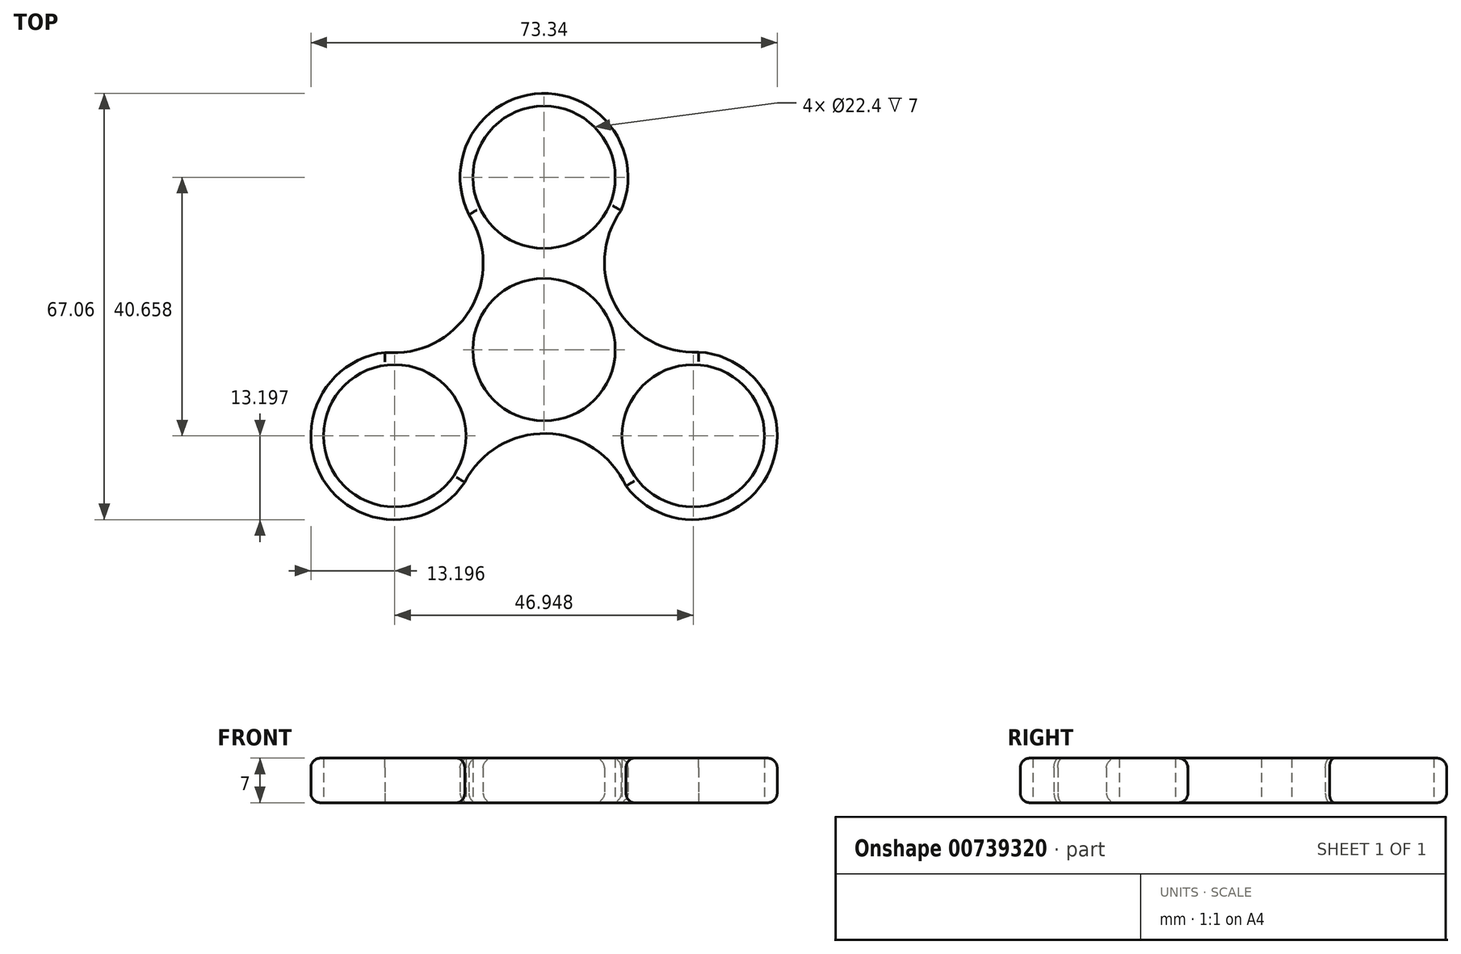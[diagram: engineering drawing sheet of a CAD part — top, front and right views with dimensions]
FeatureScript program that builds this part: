
annotation { "Feature Type Name" : "Feature", "Feature Type Description" : "" }
export const myFeature = defineFeature(function(context is Context, id is Id, definition is map)
    precondition{}
    {
        {
            var Q0;
            Q0=qCreatedBy(makeId("Top.planeOp"),FACE);
            var sketch = newSketch(context, id + "F0", { "sketchPlane" : qUnion([Q0])});
            skCircle(sketch, "E0", {"center": v(0, 0) * mm, "radius": 11.2 * mm});
            skArc(sketch, "E1", {"start": v(-11.26, 6.88) * mm, "mid": v(-11.45, 6.57) * mm, "end": v(-11.62, 6.26) * mm});
            skCircle(sketch, "E2", {"center": v(0, 27.1) * mm, "radius": 11.2 * mm});
            skArc(sketch, "E3", {"start": v(10.69, 19.36) * mm, "mid": v(0.33, 40.3) * mm, "end": v(-11.06, 19.9) * mm});
            skArc(sketch, "E4.1.0", {"start": v(-22.1, -0.42) * mm, "mid": v(-35.07, -19.86) * mm, "end": v(-11.7, -19.53) * mm});
            skCircle(sketch, "E4.1.1", {"center": v(-23.47, -13.55) * mm, "radius": 11.2 * mm});
            skArc(sketch, "E4.2.0", {"start": v(11.42, -18.94) * mm, "mid": v(34.74, -20.44) * mm, "end": v(22.77, -0.37) * mm});
            skCircle(sketch, "E4.2.1", {"center": v(23.47, -13.55) * mm, "radius": 11.2 * mm});
            skArc(sketch, "E5", {"start": v(12.13, 21.9) * mm, "mid": v(11.23, 6.94) * mm, "end": v(24.3, -0.38) * mm});
            skArc(sketch, "E6.1.0", {"start": v(-25.02, -0.44) * mm, "mid": v(-11.62, 6.25) * mm, "end": v(-11.82, 21.23) * mm});
            skArc(sketch, "E6.2.0", {"start": v(12.9, -21.45) * mm, "mid": v(0.4, -13.2) * mm, "end": v(-12.48, -20.85) * mm});
            skLineSegment(sketch, "E7", {"start": v(-13.72, -8.05) * mm, "end": v(-11.36, -6.72) * mm, "construction": true});
            skArc(sketch, "E8.trimOffspring", {"start": v(11.62, 6.25) * mm, "mid": v(11.43, 6.6) * mm, "end": v(11.23, 6.94) * mm});
            skLineSegment(sketch, "E9.trimOffspring", {"start": v(9.88, 5.27) * mm, "end": v(11.63, 6.26) * mm, "construction": true});
            skArc(sketch, "E10.trimOffspring", {"start": v(-0.33, -13.2) * mm, "mid": v(0.03, -13.2) * mm, "end": v(0.4, -13.2) * mm});
            skSolve(sketch);
        }
        {
            var Q0;
            Q0=makeQuery(id+"F0.imprint","IMPRINT",FACE,{"disambiguationData":[TD([[makeQuery(id+"F0.imprint","IMPRINT",EDGE,{"derivedFrom":sQuery(id+"F0.wireOp",EDGE,"E0")}),-1.0]])]});
            extrude(context, id + "F1", {"entities" : qUnion([Q0]), "depth" : 7 * mm, "offsetDistance" : 25 * mm});
        }
        {
            var Q0;
            Q0=makeQuery(id+"F1.opExtrude","CAP_EDGE",EDGE,{"disambiguationData":[OSD([sQuery(id+"F0.wireOp",EDGE,"E4.1.0")])],"isStart":false});
            var Q1;
            Q1=makeQuery(id+"F1.opExtrude","CAP_EDGE",EDGE,{"disambiguationData":[OSD([sQuery(id+"F0.wireOp",EDGE,"E6.1.0")])],"isStart":false});
            var Q2;
            Q2=makeQuery(id+"F1.opExtrude","CAP_EDGE",EDGE,{"disambiguationData":[OSD([sQuery(id+"F0.wireOp",EDGE,"E3")])],"isStart":false});
            var Q3;
            Q3=makeQuery(id+"F1.opExtrude","CAP_EDGE",EDGE,{"disambiguationData":[OSD([sQuery(id+"F0.wireOp",EDGE,"E5")])],"isStart":false});
            var Q4;
            Q4=makeQuery(id+"F1.opExtrude","CAP_EDGE",EDGE,{"disambiguationData":[OSD([sQuery(id+"F0.wireOp",EDGE,"E4.2.0")])],"isStart":false});
            var Q5;
            Q5=makeQuery(id+"F1.opExtrude","CAP_EDGE",EDGE,{"disambiguationData":[OSD([sQuery(id+"F0.wireOp",EDGE,"E6.2.0")])],"isStart":false});
            fillet(context, id + "F2", {"entities" : qUnion([Q0, Q1, Q2, Q3, Q4, Q5]), "radius" : 1.5 * mm, "tangentPropagation" : true, "allowEdgeOverflow" : false});
        }
        {
            var Q0;
            Q0=makeQuery(id+"F1.opExtrude","CAP_EDGE",EDGE,{"disambiguationData":[OSD([sQuery(id+"F0.wireOp",EDGE,"E4.2.0")])],"isStart":true});
            var Q1;
            Q1=makeQuery(id+"F1.opExtrude","CAP_EDGE",EDGE,{"disambiguationData":[OSD([sQuery(id+"F0.wireOp",EDGE,"E5")])],"isStart":true});
            var Q2;
            Q2=makeQuery(id+"F1.opExtrude","CAP_EDGE",EDGE,{"disambiguationData":[OSD([sQuery(id+"F0.wireOp",EDGE,"E3")])],"isStart":true});
            var Q3;
            Q3=makeQuery(id+"F1.opExtrude","CAP_EDGE",EDGE,{"disambiguationData":[OSD([sQuery(id+"F0.wireOp",EDGE,"E6.1.0")])],"isStart":true});
            var Q4;
            Q4=makeQuery(id+"F1.opExtrude","CAP_EDGE",EDGE,{"disambiguationData":[OSD([sQuery(id+"F0.wireOp",EDGE,"E4.1.0")])],"isStart":true});
            var Q5;
            Q5=makeQuery(id+"F1.opExtrude","CAP_EDGE",EDGE,{"disambiguationData":[OSD([sQuery(id+"F0.wireOp",EDGE,"E6.2.0")])],"isStart":true});
            fillet(context, id + "F3", {"entities" : qUnion([Q0, Q1, Q2, Q3, Q4, Q5]), "radius" : 1.5 * mm, "tangentPropagation" : true, "allowEdgeOverflow" : false});
        }
    });
